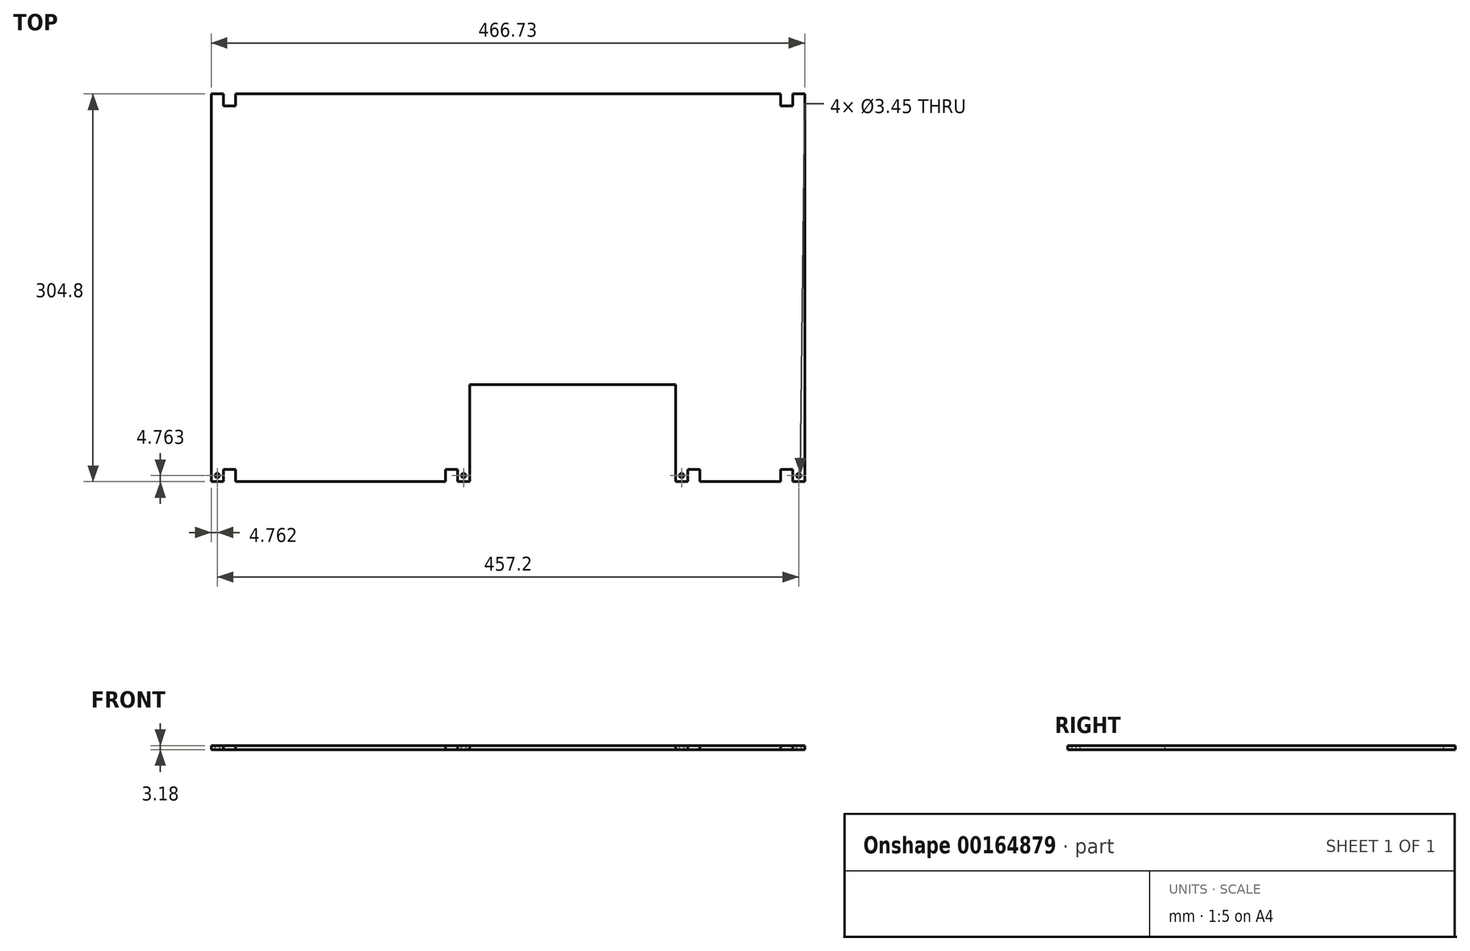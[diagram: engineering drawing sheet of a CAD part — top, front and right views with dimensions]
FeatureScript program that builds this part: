
annotation { "Feature Type Name" : "Feature", "Feature Type Description" : "" }
export const myFeature = defineFeature(function(context is Context, id is Id, definition is map)
    precondition{}
    {
        {
            var Q0;
            Q0=qCreatedBy(makeId("Top.planeOp"),FACE);
            var sketch = newSketch(context, id + "F0", { "sketchPlane" : qUnion([Q0])});
            skLineSegment(sketch, "E0.bottom", {"start": v(0, 0) * mm, "end": v(161.93, 0) * mm, "construction": true});
            skLineSegment(sketch, "E0.top", {"start": v(0, 76.2) * mm, "end": v(161.93, 76.2) * mm});
            skLineSegment(sketch, "E0.left", {"start": v(0, 0) * mm, "end": v(0, 76.2) * mm});
            skLineSegment(sketch, "E0.right", {"start": v(161.93, 0) * mm, "end": v(161.93, 76.2) * mm});
            skLineSegment(sketch, "E1", {"start": v(0, 0) * mm, "end": v(-9.52, 0) * mm});
            skLineSegment(sketch, "E2.bottom", {"start": v(-9.52, 0) * mm, "end": v(-19.05, 0) * mm, "construction": true});
            skLineSegment(sketch, "E2.top", {"start": v(-9.52, 9.53) * mm, "end": v(-19.05, 9.53) * mm});
            skLineSegment(sketch, "E2.left", {"start": v(-9.52, 0) * mm, "end": v(-9.52, 9.53) * mm});
            skLineSegment(sketch, "E2.right", {"start": v(-19.05, 0) * mm, "end": v(-19.05, 9.53) * mm});
            skLineSegment(sketch, "E3", {"start": v(161.93, 0) * mm, "end": v(171.45, 0) * mm});
            skLineSegment(sketch, "E4.bottom", {"start": v(171.45, 0) * mm, "end": v(180.98, 0) * mm, "construction": true});
            skLineSegment(sketch, "E4.top", {"start": v(171.45, 9.53) * mm, "end": v(180.98, 9.53) * mm});
            skLineSegment(sketch, "E4.left", {"start": v(171.45, 0) * mm, "end": v(171.45, 9.53) * mm});
            skLineSegment(sketch, "E4.right", {"start": v(180.98, 0) * mm, "end": v(180.98, 9.53) * mm});
            skLineSegment(sketch, "E5", {"start": v(180.98, 0) * mm, "end": v(244.47, 0) * mm});
            skLineSegment(sketch, "E6.bottom", {"start": v(244.47, 0) * mm, "end": v(254, 0) * mm, "construction": true});
            skLineSegment(sketch, "E6.top", {"start": v(244.47, 9.53) * mm, "end": v(254, 9.53) * mm});
            skLineSegment(sketch, "E6.left", {"start": v(244.47, 0) * mm, "end": v(244.47, 9.53) * mm});
            skLineSegment(sketch, "E6.right", {"start": v(254, 0) * mm, "end": v(254, 9.53) * mm});
            skLineSegment(sketch, "E7", {"start": v(254, 0) * mm, "end": v(263.53, 0) * mm});
            skLineSegment(sketch, "E8", {"start": v(263.53, 0) * mm, "end": v(263.52, 304.8) * mm});
            skLineSegment(sketch, "E9", {"start": v(-9.52, 4.76) * mm, "end": v(0, 4.76) * mm, "construction": true});
            skLineSegment(sketch, "E10", {"start": v(171.45, 4.76) * mm, "end": v(161.93, 4.76) * mm, "construction": true});
            skLineSegment(sketch, "E11", {"start": v(-19.05, 0) * mm, "end": v(-184.15, 0) * mm});
            skLineSegment(sketch, "E12.bottom", {"start": v(-184.15, 0) * mm, "end": v(-193.68, 0) * mm, "construction": true});
            skLineSegment(sketch, "E12.top", {"start": v(-184.15, 9.52) * mm, "end": v(-193.68, 9.52) * mm});
            skLineSegment(sketch, "E12.left", {"start": v(-184.15, 0) * mm, "end": v(-184.15, 9.52) * mm});
            skLineSegment(sketch, "E12.right", {"start": v(-193.68, 0) * mm, "end": v(-193.68, 9.52) * mm});
            skLineSegment(sketch, "E13", {"start": v(-193.68, 0) * mm, "end": v(-203.2, 0) * mm});
            skLineSegment(sketch, "E14", {"start": v(-203.2, 0) * mm, "end": v(-203.2, 304.8) * mm});
            skLineSegment(sketch, "E15", {"start": v(-193.68, 4.76) * mm, "end": v(-203.2, 4.76) * mm, "construction": true});
            skLineSegment(sketch, "E16", {"start": v(254, 4.76) * mm, "end": v(263.53, 4.76) * mm, "construction": true});
            skLineSegment(sketch, "E17", {"start": v(-203.2, 304.8) * mm, "end": v(-193.68, 304.8) * mm});
            skLineSegment(sketch, "E18.bottom", {"start": v(-193.68, 304.8) * mm, "end": v(-184.15, 304.8) * mm, "construction": true});
            skLineSegment(sketch, "E18.top", {"start": v(-193.68, 295.27) * mm, "end": v(-184.15, 295.27) * mm});
            skLineSegment(sketch, "E18.left", {"start": v(-193.68, 304.8) * mm, "end": v(-193.68, 295.27) * mm});
            skLineSegment(sketch, "E18.right", {"start": v(-184.15, 304.8) * mm, "end": v(-184.15, 295.27) * mm});
            skLineSegment(sketch, "E19", {"start": v(263.52, 304.8) * mm, "end": v(254, 304.8) * mm});
            skLineSegment(sketch, "E20.bottom", {"start": v(254, 304.8) * mm, "end": v(244.47, 304.8) * mm, "construction": true});
            skLineSegment(sketch, "E20.top", {"start": v(254, 295.28) * mm, "end": v(244.47, 295.28) * mm});
            skLineSegment(sketch, "E20.left", {"start": v(254, 304.8) * mm, "end": v(254, 295.28) * mm});
            skLineSegment(sketch, "E20.right", {"start": v(244.47, 304.8) * mm, "end": v(244.47, 295.28) * mm});
            skCircle(sketch, "E21", {"center": v(-198.44, 4.76) * mm, "radius": 1.73 * mm});
            skCircle(sketch, "E22", {"center": v(-4.76, 4.76) * mm, "radius": 1.73 * mm});
            skCircle(sketch, "E23", {"center": v(166.69, 4.76) * mm, "radius": 1.73 * mm});
            skCircle(sketch, "E24", {"center": v(258.76, 4.76) * mm, "radius": 1.73 * mm});
            skLineSegment(sketch, "E25", {"start": v(-184.15, 304.8) * mm, "end": v(244.47, 304.8) * mm});
            skSolve(sketch);
        }
        {
            var Q0;
            Q0 = qSketchRegion(id + "F0", true);
            extrude(context, id + "F1", {"entities" : qUnion([Q0]), "depth" : 3.17 * mm});
        }
    });
